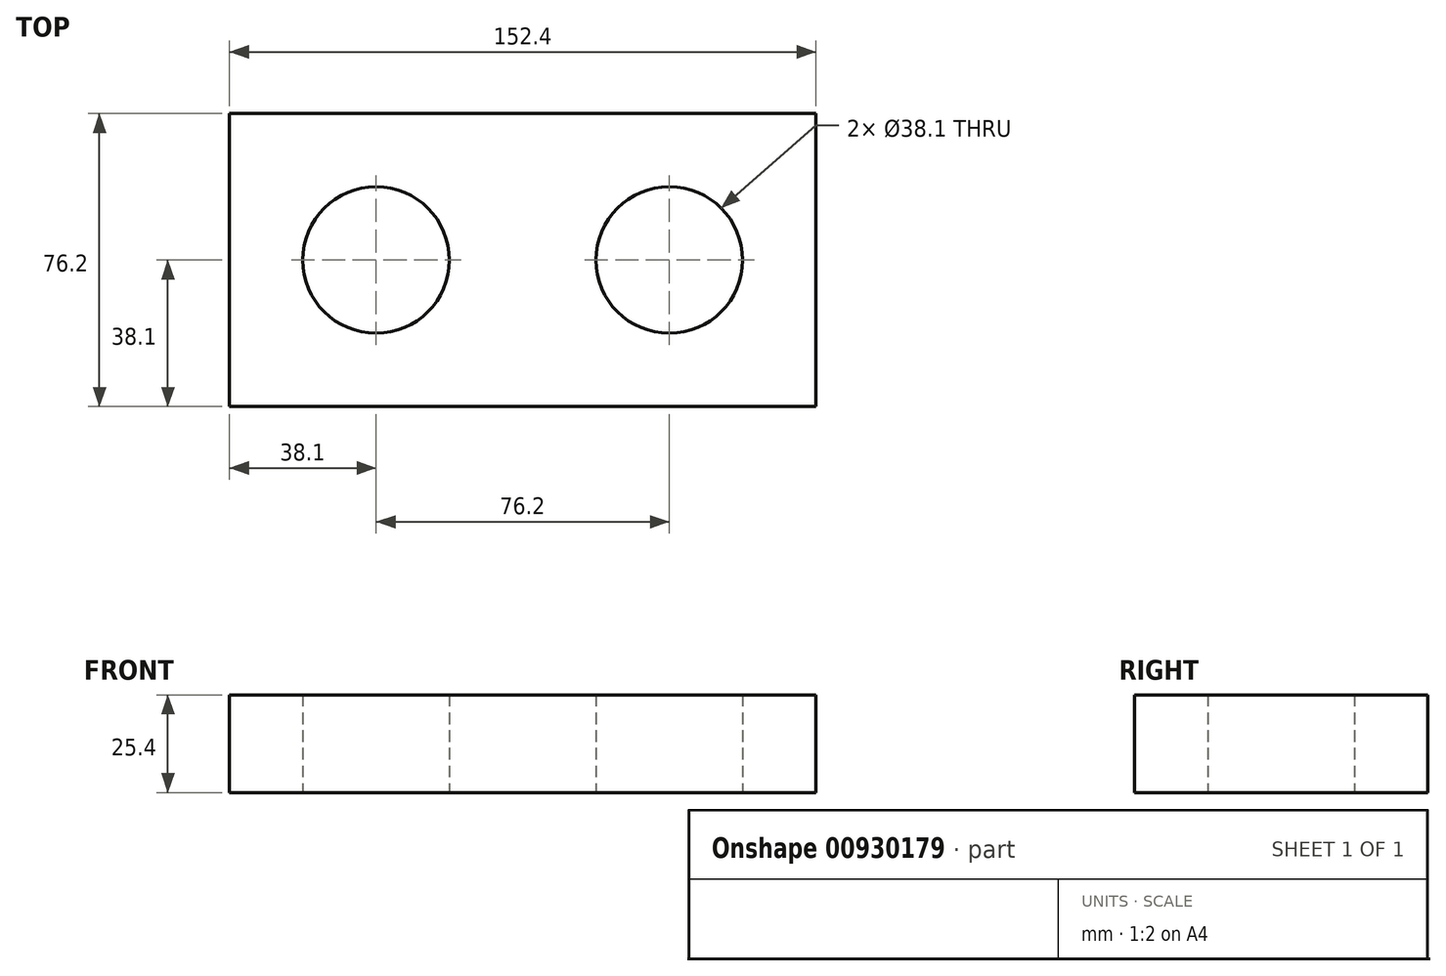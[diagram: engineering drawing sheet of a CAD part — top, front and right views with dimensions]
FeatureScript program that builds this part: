
annotation { "Feature Type Name" : "Feature", "Feature Type Description" : "" }
export const myFeature = defineFeature(function(context is Context, id is Id, definition is map)
    precondition{}
    {
        {
            var Q0;
            Q0=qCreatedBy(makeId("Top.planeOp"),FACE);
            var sketch = newSketch(context, id + "F0", { "sketchPlane" : qUnion([Q0])});
            skLineSegment(sketch, "E0.bottom", {"start": v(76.2, 38.1) * mm, "end": v(-76.2, 38.1) * mm});
            skLineSegment(sketch, "E0.top", {"start": v(76.2, -38.1) * mm, "end": v(-76.2, -38.1) * mm});
            skLineSegment(sketch, "E0.left", {"start": v(76.2, 38.1) * mm, "end": v(76.2, -38.1) * mm});
            skLineSegment(sketch, "E0.right", {"start": v(-76.2, 38.1) * mm, "end": v(-76.2, -38.1) * mm});
            skPoint(sketch, "E0.middle", {"position": v(0, 0) * mm});
            skLineSegment(sketch, "E1", {"start": v(-38.1, 38.1) * mm, "end": v(-38.1, -38.1) * mm, "construction": true});
            skLineSegment(sketch, "E2", {"start": v(38.1, 38.1) * mm, "end": v(38.1, -38.1) * mm, "construction": true});
            skLineSegment(sketch, "E3", {"start": v(-76.2, 0) * mm, "end": v(76.2, 0) * mm, "construction": true});
            skCircle(sketch, "E4", {"center": v(-38.1, 0) * mm, "radius": 19.05 * mm});
            skPoint(sketch, "E5", {"position": v(-38.1, 19.05) * mm});
            skCircle(sketch, "E6", {"center": v(38.1, 0) * mm, "radius": 19.05 * mm});
            skPoint(sketch, "E7", {"position": v(38.1, 19.05) * mm});
            skSolve(sketch);
        }
        {
            var Q0;
            Q0 = qSketchRegion(id + "F0", true);
            extrude(context, id + "F1", {"entities" : qUnion([Q0]), "depth" : 25.4 * mm, "offsetDistance" : 25.4 * mm});
        }
    });
